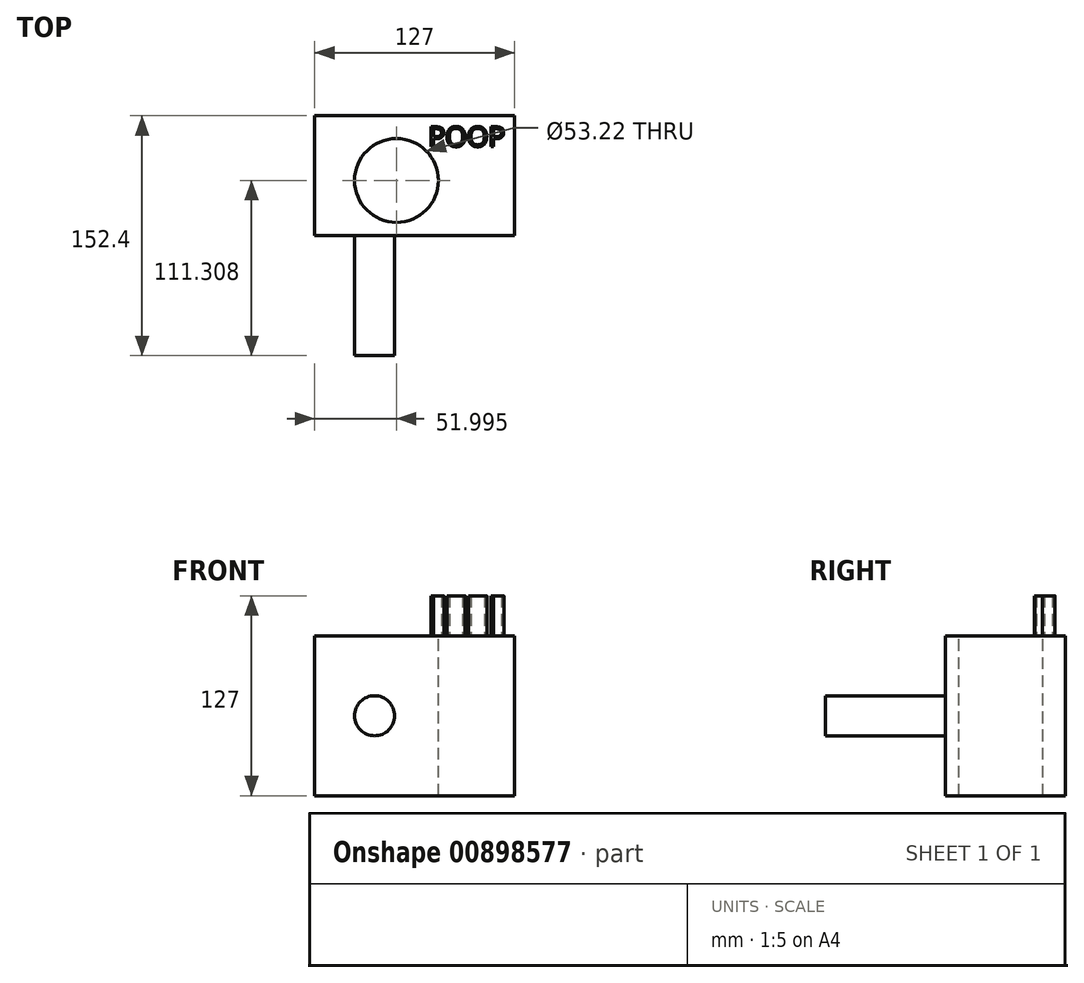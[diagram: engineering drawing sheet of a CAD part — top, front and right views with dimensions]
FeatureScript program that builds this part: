
annotation { "Feature Type Name" : "Feature", "Feature Type Description" : "" }
export const myFeature = defineFeature(function(context is Context, id is Id, definition is map)
    precondition{}
    {
        {
            var Q0;
            Q0=qCreatedBy(makeId("Top.planeOp"),FACE);
            var sketch = newSketch(context, id + "F0", { "sketchPlane" : qUnion([Q0])});
            skLineSegment(sketch, "E0.bottom", {"start": v(63.5, -38.1) * mm, "end": v(-63.5, -38.1) * mm});
            skLineSegment(sketch, "E0.top", {"start": v(63.5, 38.1) * mm, "end": v(-63.5, 38.1) * mm});
            skLineSegment(sketch, "E0.left", {"start": v(63.5, -38.1) * mm, "end": v(63.5, 38.1) * mm});
            skLineSegment(sketch, "E0.right", {"start": v(-63.5, -38.1) * mm, "end": v(-63.5, 38.1) * mm});
            skPoint(sketch, "E0.middle", {"position": v(0, 0) * mm});
            skSolve(sketch);
        }
        {
            var Q0;
            Q0 = qSketchRegion(id + "F0", true);
            extrude(context, id + "F1", {"entities" : qUnion([Q0]), "depth" : 101.6 * mm, "offsetDistance" : 25.4 * mm});
        }
        {
            var Q0;
            Q0=makeQuery(id+"F1.opExtrude","SWEPT_FACE",FACE,{"disambiguationData":[OSD([sQuery(id+"F0.wireOp",EDGE,"E0.bottom")])]});
            var sketch = newSketch(context, id + "F2", { "sketchPlane" : qUnion([Q0])});
            skCircle(sketch, "E1", {"center": v(-25.4, 50.8) * mm, "radius": 12.7 * mm});
            skSolve(sketch);
        }
        {
            var Q0;
            Q0 = qSketchRegion(id + "F2", true);
            extrude(context, id + "F3", {"entities" : qUnion([Q0]), "operationType" : NewBodyOperationType.ADD, "depth" : 76.2 * mm, "offsetDistance" : 25.4 * mm});
        }
        {
            var Q0;
            Q0=makeQuery(id+"F1.opExtrude","CAP_FACE",FACE,{"disambiguationData":[OSD([sQuery(id+"F0.wireOp",EDGE,"E0.bottom"),sQuery(id+"F0.wireOp",EDGE,"E0.top"),sQuery(id+"F0.wireOp",EDGE,"E0.left"),sQuery(id+"F0.wireOp",EDGE,"E0.right")])],"isStart":false});
            var sketch = newSketch(context, id + "F4", { "sketchPlane" : qUnion([Q0])});
            skCircle(sketch, "E2", {"center": v(-11.5, -3) * mm, "radius": 26.61 * mm});
            skSolve(sketch);
        }
        {
            var Q0;
            Q0 = qSketchRegion(id + "F4", true);
            extrude(context, id + "F5", {"entities" : qUnion([Q0]), "operationType" : NewBodyOperationType.REMOVE, "endBound" : BoundingType.THROUGH_ALL, "oppositeDirection" : true, "depth" : 25.4 * mm, "offsetDistance" : 25.4 * mm});
        }
        {
            var Q0;
            Q0=makeQuery(id+"F1.opExtrude","CAP_FACE",FACE,{"disambiguationData":[OSD([sQuery(id+"F0.wireOp",EDGE,"E0.bottom"),sQuery(id+"F0.wireOp",EDGE,"E0.top"),sQuery(id+"F0.wireOp",EDGE,"E0.left"),sQuery(id+"F0.wireOp",EDGE,"E0.right")])],"isStart":false});
            var sketch = newSketch(context, id + "F6", { "sketchPlane" : qUnion([Q0])});
            skText(sketch, "E3", { "text": "POOP\n", "fontName": "OpenSans-Regular.ttf"});
            const initialGuessF6  = {"E3": [0.00882, 0.01853, 1, 0, 0.0127]};
            skSetInitialGuess(sketch, initialGuessF6);
            skSolve(sketch);
        }
        {
            var Q0;
            Q0 = qSketchRegion(id + "F6", true);
            extrude(context, id + "F7", {"entities" : qUnion([Q0]), "operationType" : NewBodyOperationType.ADD, "depth" : 25.4 * mm, "offsetDistance" : 25.4 * mm});
        }
    });
